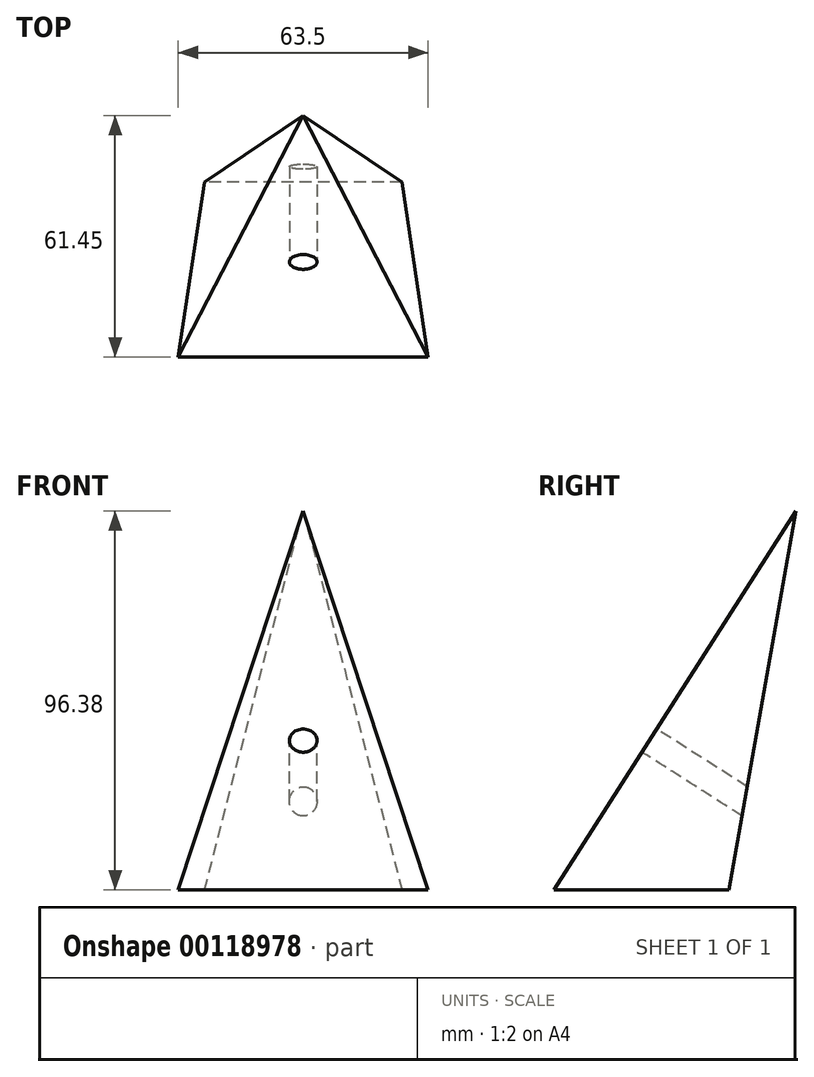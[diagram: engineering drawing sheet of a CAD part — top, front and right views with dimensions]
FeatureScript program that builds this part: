
annotation { "Feature Type Name" : "Feature", "Feature Type Description" : "" }
export const myFeature = defineFeature(function(context is Context, id is Id, definition is map)
    precondition{}
    {
        {
            var Q0;
            Q0=qCreatedBy(makeId("Right.planeOp"),FACE);
            var sketch = newSketch(context, id + "F0", { "sketchPlane" : qUnion([Q0])});
            skLineSegment(sketch, "E0", {"start": v(-25.64, 0) * mm, "end": v(18.81, 0) * mm});
            skLineSegment(sketch, "E1", {"start": v(-25.64, 0) * mm, "end": v(35.8, 96.38) * mm});
            skLineSegment(sketch, "E2", {"start": v(35.8, 96.38) * mm, "end": v(18.81, 0) * mm});
            skSolve(sketch);
        }
        {
            var Q0;
            Q0=qSketchRegion(id+"F0",true);
            extrude(context, id + "F1", {"entities" : qUnion([Q0]), "depth" : 63.5 * mm});
        }
        {
            var Q0;
            Q0=makeQuery(id+"F1.opExtrude","SWEPT_FACE",FACE,{"disambiguationData":[OSD([sQuery(id+"F0.wireOp",EDGE,"E1")])]});
            var sketch = newSketch(context, id + "F2", { "sketchPlane" : qUnion([Q0])});
            skLineSegment(sketch, "E3", {"start": v(0, -13.78) * mm, "end": v(0, 100.52) * mm});
            skLineSegment(sketch, "E4", {"start": v(0, 100.52) * mm, "end": v(63.5, 100.52) * mm});
            skLineSegment(sketch, "E5", {"start": v(63.5, 100.52) * mm, "end": v(63.5, -13.78) * mm});
            skLineSegment(sketch, "E6", {"start": v(63.5, -13.78) * mm, "end": v(31.75, 100.52) * mm});
            skLineSegment(sketch, "E7", {"start": v(31.75, 100.52) * mm, "end": v(0, -13.78) * mm});
            skSolve(sketch);
        }
        {
            var Q0;
            Q0 = qSketchRegion(id + "F2", true);
            extrude(context, id + "F3", {"entities" : qUnion([Q0]), "operationType" : NewBodyOperationType.REMOVE, "endBound" : BoundingType.THROUGH_ALL, "oppositeDirection" : true, "depth" : 25.4 * mm});
        }
        {
            var Q0;
            Q0=makeQuery(id+"F1.opExtrude","SWEPT_FACE",FACE,{"disambiguationData":[OSD([sQuery(id+"F0.wireOp",EDGE,"E1")])]});
            var sketch = newSketch(context, id + "F4", { "sketchPlane" : qUnion([Q0])});
            skLineSegment(sketch, "E8", {"start": v(31.75, -13.78) * mm, "end": v(31.75, 100.52) * mm, "construction": true});
            skCircle(sketch, "E9", {"center": v(31.75, 31.25) * mm, "radius": 3.5 * mm});
            skSolve(sketch);
        }
        {
            var Q0;
            Q0=qSketchRegion(id+"F4",true);
            extrude(context, id + "F5", {"entities" : qUnion([Q0]), "operationType" : NewBodyOperationType.REMOVE, "endBound" : BoundingType.THROUGH_ALL, "oppositeDirection" : true, "depth" : 28.37 * mm});
        }
    });
